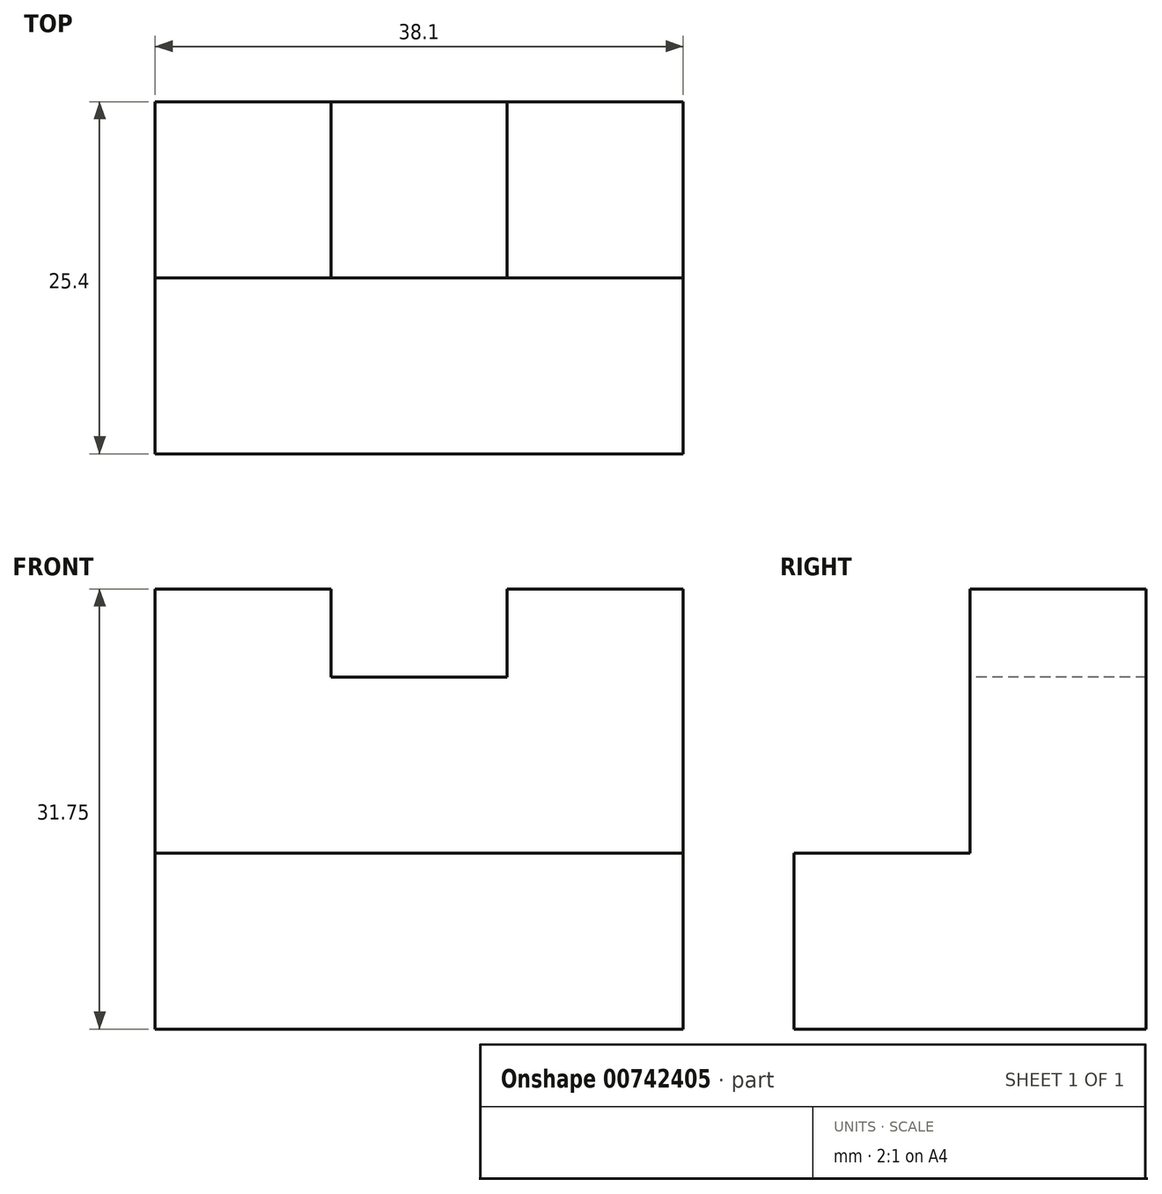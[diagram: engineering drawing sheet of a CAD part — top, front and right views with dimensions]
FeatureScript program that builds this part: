
annotation { "Feature Type Name" : "Feature", "Feature Type Description" : "" }
export const myFeature = defineFeature(function(context is Context, id is Id, definition is map)
    precondition{}
    {
        {
            var Q0;
            Q0=qCreatedBy(makeId("Front.planeOp"),FACE);
            var sketch = newSketch(context, id + "F0", { "sketchPlane" : qUnion([Q0])});
            skLineSegment(sketch, "E0", {"start": v(0, 0) * mm, "end": v(0, 31.75) * mm});
            skLineSegment(sketch, "E1", {"start": v(0, 31.75) * mm, "end": v(38.1, 31.75) * mm});
            skLineSegment(sketch, "E2", {"start": v(38.1, 31.75) * mm, "end": v(38.1, 0) * mm});
            skLineSegment(sketch, "E3", {"start": v(0, 0) * mm, "end": v(38.1, 0) * mm});
            skSolve(sketch);
        }
        {
            var Q0;
            Q0 = qSketchRegion(id + "F0", true);
            extrude(context, id + "F1", {"entities" : qUnion([Q0]), "depth" : 25.4 * mm, "offsetDistance" : 25.4 * mm});
        }
        {
            var Q0;
            Q0=makeQuery(id+"F1.opExtrude","CAP_FACE",FACE,{"disambiguationData":[OSD([sQuery(id+"F0.wireOp",EDGE,"E0"),sQuery(id+"F0.wireOp",EDGE,"E1"),sQuery(id+"F0.wireOp",EDGE,"E2"),sQuery(id+"F0.wireOp",EDGE,"E3")])],"isStart":false});
            var sketch = newSketch(context, id + "F2", { "sketchPlane" : qUnion([Q0])});
            skLineSegment(sketch, "E4", {"start": v(0, 12.7) * mm, "end": v(38.1, 12.7) * mm});
            skSolve(sketch);
        }
        {
            var Q0;
            {var subQ0=sQuery(id+"F2.wireOp",EDGE,"E4");Q0=makeQuery(id+"F2.imprint","IMPRINT",FACE,{"disambiguationData":[TD([[makeQuery(id+"F2.imprint","IMPRINT",EDGE,{"derivedFrom":subQ0}),1.0]])]});}
            extrude(context, id + "F3", {"entities" : qUnion([Q0]), "operationType" : NewBodyOperationType.REMOVE, "oppositeDirection" : true, "depth" : 12.7 * mm, "offsetDistance" : 25.4 * mm});
        }
        {
            var Q0;
            Q0=makeQuery(id+"F3.boolean.opBoolean","COPY",FACE,{"derivedFrom":makeQuery(id+"F3.opExtrude","CAP_FACE",FACE,{"disambiguationData":[OSD([sQuery(id+"F0.wireOp",EDGE,"E0"),sQuery(id+"F0.wireOp",EDGE,"E1"),sQuery(id+"F0.wireOp",EDGE,"E2"),sQuery(id+"F2.wireOp",EDGE,"E4")])],"isStart":false})});
            var sketch = newSketch(context, id + "F4", { "sketchPlane" : qUnion([Q0])});
            skLineSegment(sketch, "E5", {"start": v(12.7, 31.75) * mm, "end": v(12.7, 25.4) * mm});
            skLineSegment(sketch, "E6", {"start": v(11.64, 25.4) * mm, "end": v(25.4, 25.4) * mm});
            skLineSegment(sketch, "E7", {"start": v(25.4, 25.4) * mm, "end": v(25.4, 31.75) * mm});
            skSolve(sketch);
        }
        {
            var Q0;
            {var subQ0=sQuery(id+"F4.wireOp",EDGE,"E5");Q0=makeQuery(id+"F4.imprint","IMPRINT",FACE,{"disambiguationData":[TD([[makeQuery(id+"F4.imprint","IMPRINT",EDGE,{"derivedFrom":subQ0}),1.0]])]});}
            extrude(context, id + "F5", {"entities" : qUnion([Q0]), "operationType" : NewBodyOperationType.REMOVE, "endBound" : BoundingType.THROUGH_ALL, "oppositeDirection" : true, "depth" : 25.4 * mm, "offsetDistance" : 25.4 * mm});
        }
    });
